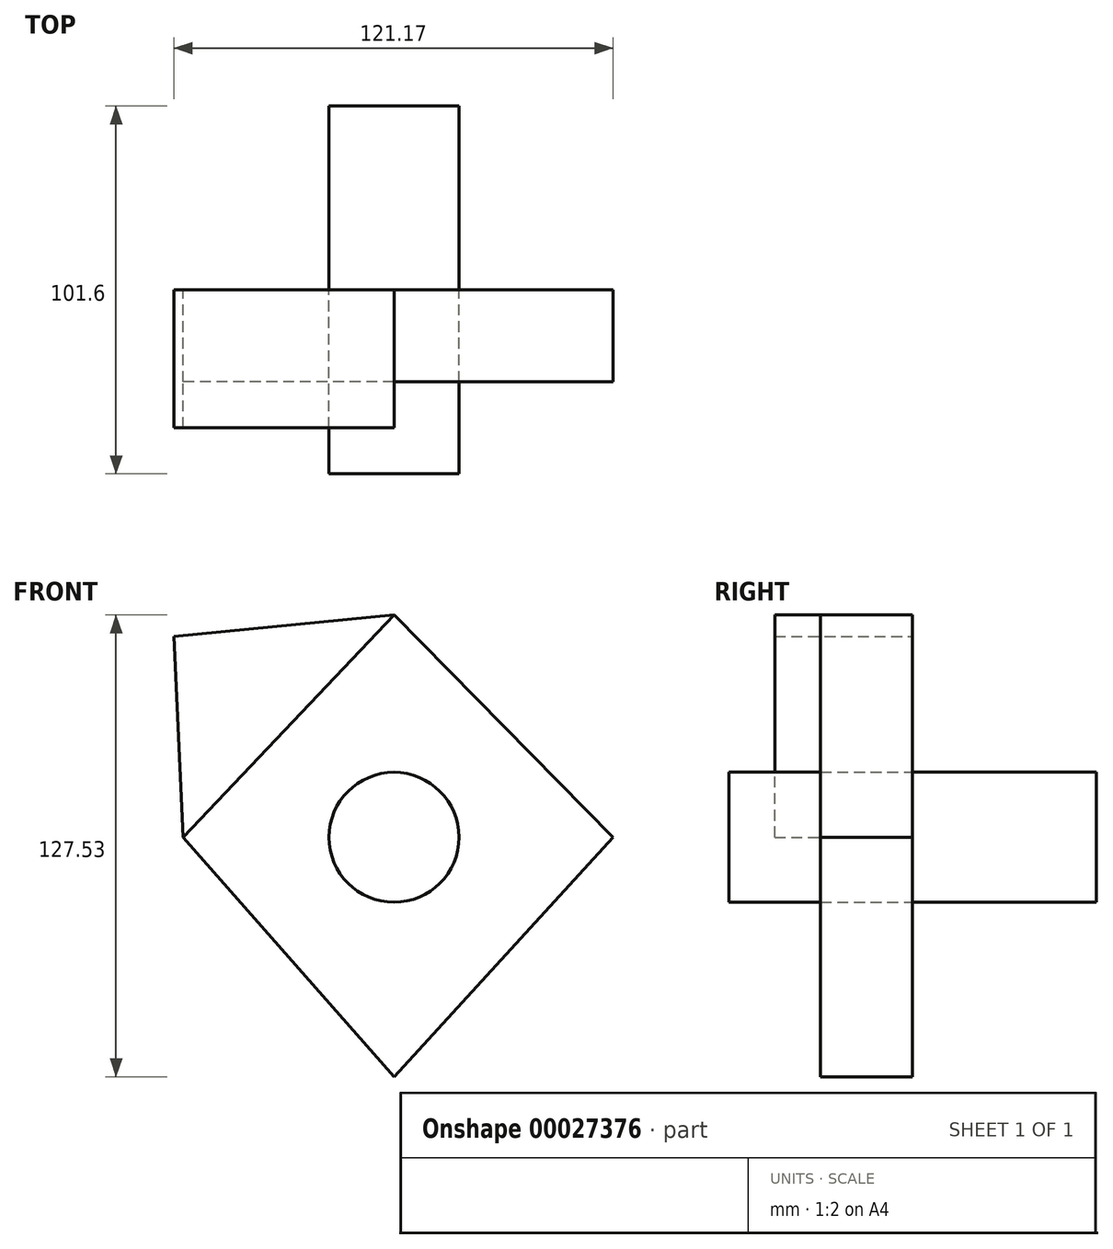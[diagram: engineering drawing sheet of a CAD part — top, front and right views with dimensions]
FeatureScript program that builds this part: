
annotation { "Feature Type Name" : "Feature", "Feature Type Description" : "" }
export const myFeature = defineFeature(function(context is Context, id is Id, definition is map)
    precondition{}
    {
        {
            var Q0;
            Q0=qCreatedBy(makeId("Front.planeOp"),FACE);
            var sketch = newSketch(context, id + "F0", { "sketchPlane" : qUnion([Q0])});
            skLineSegment(sketch, "E0", {"start": v(-58.29, 0) * mm, "end": v(0, 61.4) * mm});
            skLineSegment(sketch, "E1", {"start": v(0, 61.4) * mm, "end": v(60.45, 0) * mm});
            skLineSegment(sketch, "E2", {"start": v(60.45, 0) * mm, "end": v(0, -66.14) * mm});
            skLineSegment(sketch, "E3", {"start": v(0, -66.14) * mm, "end": v(-58.29, 0) * mm});
            skLineSegment(sketch, "E4", {"start": v(-58.29, 0) * mm, "end": v(-60.72, 55.45) * mm});
            skLineSegment(sketch, "E5", {"start": v(-60.72, 55.45) * mm, "end": v(0, 61.4) * mm});
            skCircle(sketch, "E6", {"center": v(0, 0) * mm, "radius": 17.95 * mm});
            skSolve(sketch);
        }
        {
            var Q0;
            Q0=makeQuery(id+"F0.imprint","IMPRINT",FACE,{"disambiguationData":[TD([[makeQuery(id+"F0.imprint","IMPRINT",EDGE,{"derivedFrom":sQuery(id+"F0.wireOp",EDGE,"E0")}),-1.0]])]});
            var Q1;
            Q1=makeQuery(id+"F0.imprint","IMPRINT",FACE,{"disambiguationData":[TD([[makeQuery(id+"F0.imprint","IMPRINT",EDGE,{"derivedFrom":sQuery(id+"F0.wireOp",EDGE,"E6")}),1.0]])]});
            extrude(context, id + "F1", {"entities" : qUnion([Q0, Q1]), "depth" : 25.4 * mm});
        }
        {
            var Q0;
            Q0=makeQuery(id+"F0.imprint","IMPRINT",FACE,{"disambiguationData":[TD([[makeQuery(id+"F0.imprint","IMPRINT",EDGE,{"derivedFrom":sQuery(id+"F0.wireOp",EDGE,"E0")}),1.0]])]});
            extrude(context, id + "F2", {"entities" : qUnion([Q0]), "operationType" : NewBodyOperationType.ADD, "depth" : 38.1 * mm});
        }
        {
            var Q0;
            Q0=makeQuery(id+"F0.imprint","IMPRINT",FACE,{"disambiguationData":[TD([[makeQuery(id+"F0.imprint","IMPRINT",EDGE,{"derivedFrom":sQuery(id+"F0.wireOp",EDGE,"E6")}),1.0]])]});
            extrude(context, id + "F3", {"entities" : qUnion([Q0]), "endBound" : BoundingType.SYMMETRIC, "depth" : 101.6 * mm});
        }
    });
